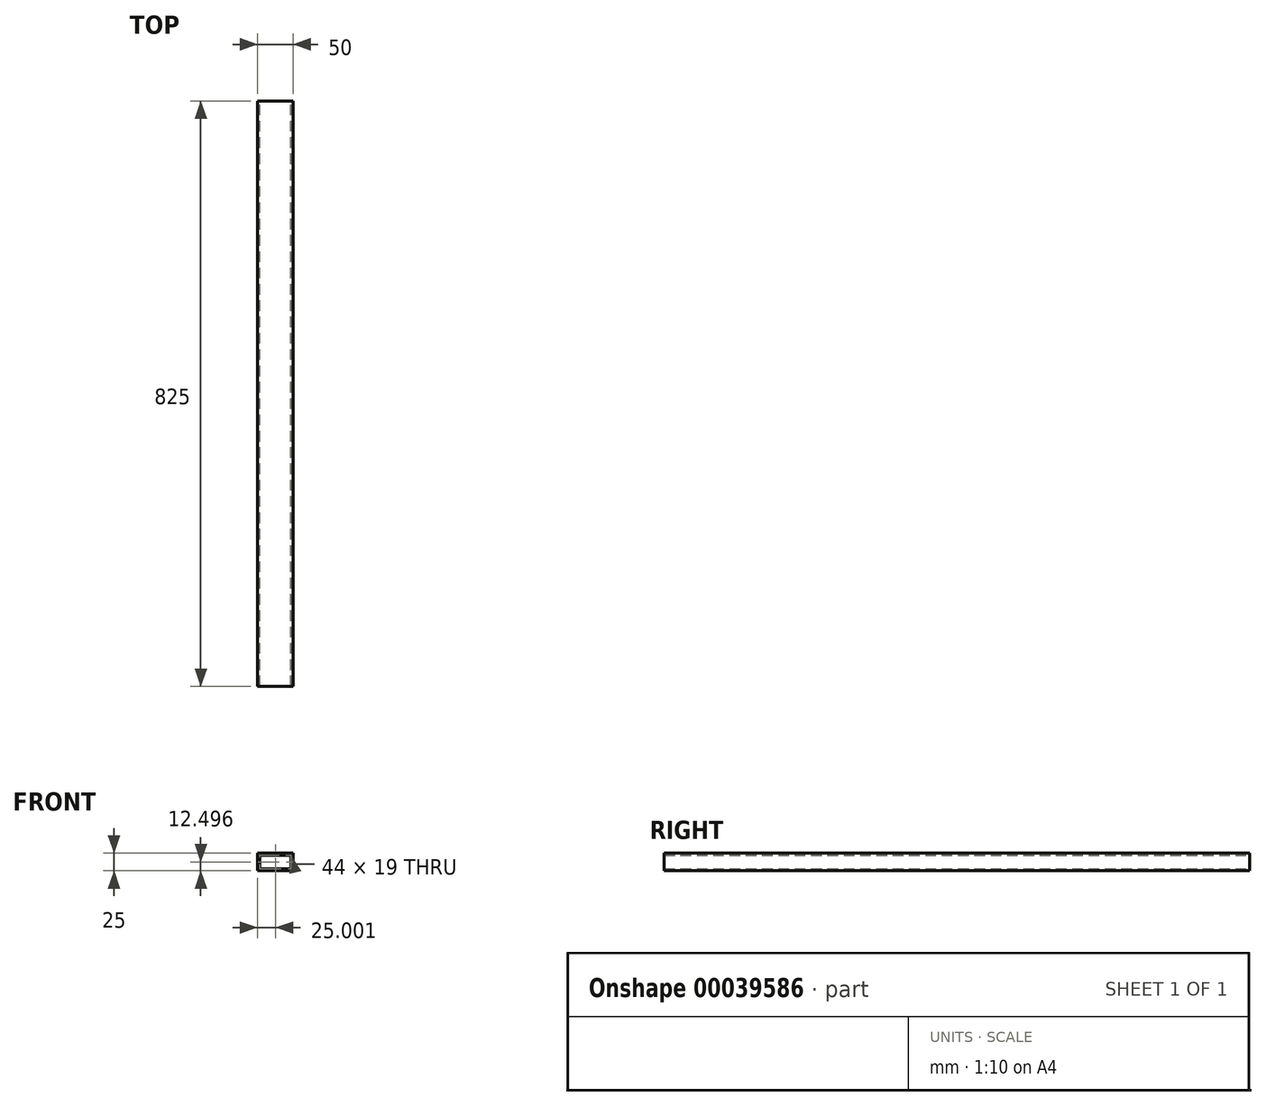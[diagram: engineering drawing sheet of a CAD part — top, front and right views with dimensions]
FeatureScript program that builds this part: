
annotation { "Feature Type Name" : "Feature", "Feature Type Description" : "" }
export const myFeature = defineFeature(function(context is Context, id is Id, definition is map)
    precondition{}
    {
        {
            var Q0;
            Q0=qCreatedBy(makeId("Front.planeOp"),FACE);
            var sketch = newSketch(context, id + "F0", { "sketchPlane" : qUnion([Q0])});
            skLineSegment(sketch, "E0.bottom", {"start": v(-49.68, 56.02) * mm, "end": v(0.32, 56.02) * mm});
            skLineSegment(sketch, "E0.top", {"start": v(-49.68, 31.02) * mm, "end": v(0.32, 31.02) * mm});
            skLineSegment(sketch, "E0.left", {"start": v(-49.68, 56.02) * mm, "end": v(-49.68, 31.02) * mm});
            skLineSegment(sketch, "E0.right", {"start": v(0.32, 56.02) * mm, "end": v(0.32, 31.02) * mm});
            skLineSegment(sketch, "E1.bottom", {"start": v(-46.68, 53.02) * mm, "end": v(-2.68, 53.02) * mm});
            skLineSegment(sketch, "E1.top", {"start": v(-46.68, 34.02) * mm, "end": v(-2.68, 34.02) * mm});
            skLineSegment(sketch, "E1.left", {"start": v(-46.68, 53.02) * mm, "end": v(-46.68, 34.02) * mm});
            skLineSegment(sketch, "E1.right", {"start": v(-2.68, 53.02) * mm, "end": v(-2.68, 34.02) * mm});
            skSolve(sketch);
        }
        {
            var Q0;
            Q0=makeQuery(id+"F0.imprint","IMPRINT",FACE,{"disambiguationData":[TD([[makeQuery(id+"F0.imprint","IMPRINT",EDGE,{"derivedFrom":sQuery(id+"F0.wireOp",EDGE,"E0.bottom")}),-1.0]])]});
            extrude(context, id + "F1", {"entities" : qUnion([Q0]), "depth" : 825 * mm});
        }
    });
